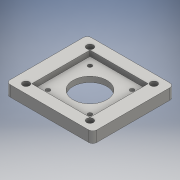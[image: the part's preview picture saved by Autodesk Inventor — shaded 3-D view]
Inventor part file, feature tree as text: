
AUTODESK INVENTOR PART (.ipt)
format: ipt  version: 2016 SP1 (Build 200210100, 210)  size: 148,480 bytes
history: native  units: mm
features: extrude x2, sketch x2, fillet x1
ambient origin geometry x8: Origin, YZ Plane, XZ Plane, XY Plane, X Axis, Y Axis, Z Axis, Center Point
bodies: Solid1 (feature_tree)
feature tree (5):
  extrude  "Extrusion1"  Depth=21.92mm
  extrude  "Extrusion2"  Depth=3.0mm
  fillet  "Fillet1"  Radius=25.0mm
  sketch  "Sketch1"  dims[d0=3.0mm d1=21.92mm]
  sketch  "Sketch2"  dims[d2=40.0mm d4=360.0deg d6=15.5mm d7=25.0mm d8=5.0mm d9=33.33mm d10=40.0mm d12=360.0deg d14=0.0mm d15=64.0mm d16=60.0mm d17=30.0mm d18=32.0mm d19=8.0mm d20=0.0mm d21=43.0mm d22=43.0mm d23=21.5mm d24=21.5mm d25=4.0mm d26=0.0mm d27=3.0mm]
